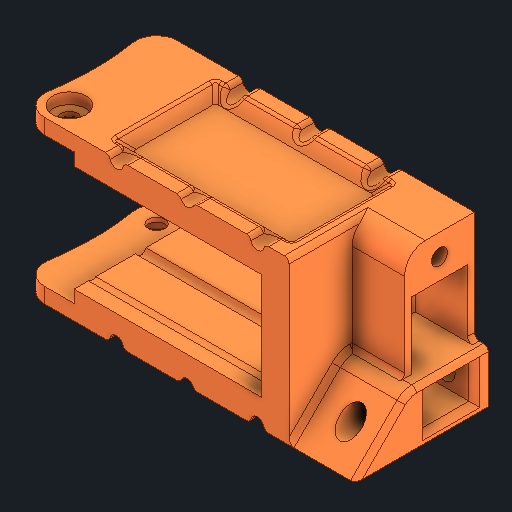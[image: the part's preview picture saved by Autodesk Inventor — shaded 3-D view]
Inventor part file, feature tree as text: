
AUTODESK INVENTOR PART (.ipt)
format: ipt  version: 2023.4 (Build 274418000, 418)  size: 768,000 bytes
history: native  units: mm
features: extrude x13, reference x12, sketch x6, projected_geometry x5, plane x3, fillet x3, other x3, chamfer x1
ambient origin geometry x8: Origin, YZ Plane, XZ Plane, XY Plane, X Axis, Y Axis, Z Axis, Center Point
bodies: Solid1 (feature_tree)
feature tree (46):
  sketch  "Sketch1"  dims[d0=65.0mm d1=0.375mm]
  plane  "Work Plane1"
  extrude  "Extrusion1"  Depth=0.375mm
  extrude  "Extrusion2"  Depth=0.375mm
  plane  "Work Plane2"
  sketch  "Sketch3"  dims[d4=29.25mm d5=0.0mm d7=5.0mm]
  extrude  "Extrusion3"  Depth=5.0mm
  extrude  "Extrusion4"  Depth=0.75mm
  extrude  "Extrusion5"  Depth=2.0mm
  extrude  "Extrusion6"  Depth=0.875mm
  extrude  "Extrusion7"  Depth=0.875mm
  plane  "Work Plane3"
  extrude  "Extrusion8"  Depth=0.875mm
  chamfer  "Chamfer1"  Distance=5.0mm
  fillet  "Fillet1"  Radius=10.15mm
  sketch  "Sketch6"  dims[d13=2.0mm d14=0.375mm d15=2.5mm d16=5.0mm d21=5.0mm d23=10.15mm d24=12.15mm d25=1.25mm d29=0.95mm d30=6.325mm d31=45.0deg d32=10.0mm d33=2.25mm d34=10.0mm d35=0.0mm d36=9.5mm d37=0.0mm d38=2.5mm d39=0.0mm d40=4.875mm d41=0.0mm d42=10.0mm d43=0.0mm d44=4.0mm d46=-2.5mm d48=8.375mm d49=0.0mm d52=1.0mm d53=2.0mm d54=45.0deg d58=3.75mm d61=6.0mm d62=3.0mm d63=2.5mm d64=0.0mm d65=2.0mm d66=0.0mm d67=2.0mm d68=0.0mm d69=2.0mm d70=0.0mm d71=0.375mm d72=0.375mm d73=2.0mm d74=0.5mm d75=2.4mm d76=2.4mm d77=2.4mm d81=15.0mm d82=1.875mm d83=0.0mm d84=1.875mm d85=0.0mm d86=28.75mm d87=1.875mm d88=2.0mm d89=45.0deg d90=0.875mm d92=5.0mm d93=5.0mm d94=0.25mm d95=6.0mm d96=0.875mm d98=2.875mm d55=0.0mm d56=0.0mm d57=0.0mm d97=0.0mm d99=0.0mm d100=0.0mm]
  extrude  "Extrusion10"  Depth=0.875mm
  extrude  "Extrusion11"  Depth=0.875mm
  extrude  "Extrusion12"  Depth=0.875mm
  extrude  "Extrusion13"  Depth=0.875mm
  extrude  "Extrusion14"  TaperAngle=45.0deg  [1 undecoded]
  fillet  "Fillet2"  Radius=10.0mm
  fillet  "Fillet3"  Radius=2.25mm
  reference  "Reference4"
  sketch  "Sketch2"  dims[d2=24.05mm d3=0.375mm]
  reference  "Reference5"
  reference  "Reference6"
  reference  "Reference7"
  reference  "Reference8"
  projected_geometry  "Projected Loop1"
  projected_geometry  "Projected Loop2"
  projected_geometry  "Projected Loop3"
  sketch  "Sketch4"  dims[d8=29.25mm d9=0.0mm d10=0.75mm]
  reference  "Reference9"
  sketch  "Sketch5"  dims[d11=2.5mm d12=2.0mm]
  projected_geometry  "Projected Loop4"
  projected_geometry  "Projected Loop5"
  reference  "Reference10"
  reference  "Reference11"
  reference  "Reference12"
  reference  "Reference13"
  reference  "Reference14"
  reference  "Reference15"
  other  "XYZ Stage V5.iam"
  other  "Z Stage Part V5:1"
  parser-record x1  (decoder bookkeeping rows leaked as tree rows — omitted from the tree; the rows remain in map.json)
note: 1 required parameter value undecoded (feature->parameter linkage not recoverable at this tier; creation-order binding heuristic only, values carry confidence <= 0.55)
note: 1 file-system path scrubbed to <path> (originals preserved in map.json)
